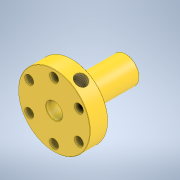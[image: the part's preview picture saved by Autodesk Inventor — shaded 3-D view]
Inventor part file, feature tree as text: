
AUTODESK INVENTOR PART (.ipt)
format: ipt  version: 2020 (Build 240168000, 168)  size: 172,544 bytes
history: native  units: mm
features: sketch x3, hole x2, plane x2, revolve x1, pattern_circular x1, chamfer x1
ambient origin geometry x8: Origin, YZ Plane, XZ Plane, XY Plane, X Axis, Y Axis, Z Axis, Center Point
bodies: Solid1 (feature_tree)
feature tree (10):
  revolve  "Revolution1"  [1 undecoded]
  hole  "Hole1"  [1 undecoded]
  pattern_circular  "Circular Pattern1"  Count=4  [1 undecoded]
  plane  "Work Plane2"
  hole  "Hole2"  [1 undecoded]
  chamfer  "Chamfer1"  Distance=60.0mm Angle=360.0deg
  sketch  "Sketch1"  dims[d0=9.0mm d1=15.0mm]
  sketch  "Sketch2"  dims[d2=30.0mm d3=10.0mm d4=40.0mm]
  plane  "Work Plane1"
  sketch  "Sketch3"  dims[d5=90.0deg d6=16.0mm d7=5.0mm d8=6.0mm d9=4.0mm d10=2.0mm d11=90.0deg d12=8.0mm d13=20.594885mm d14=60.0mm d15=360.0deg d17=60.0deg d18=6.647mm d19=10.0mm d20=4.0mm d21=2.0mm d22=90.0deg d23=20.2mm d24=20.594885mm d25=0.2mm d26=2.0mm d27=45.0deg]
note: 4 required parameter values undecoded (feature->parameter linkage not recoverable at this tier; creation-order binding heuristic only, values carry confidence <= 0.55)